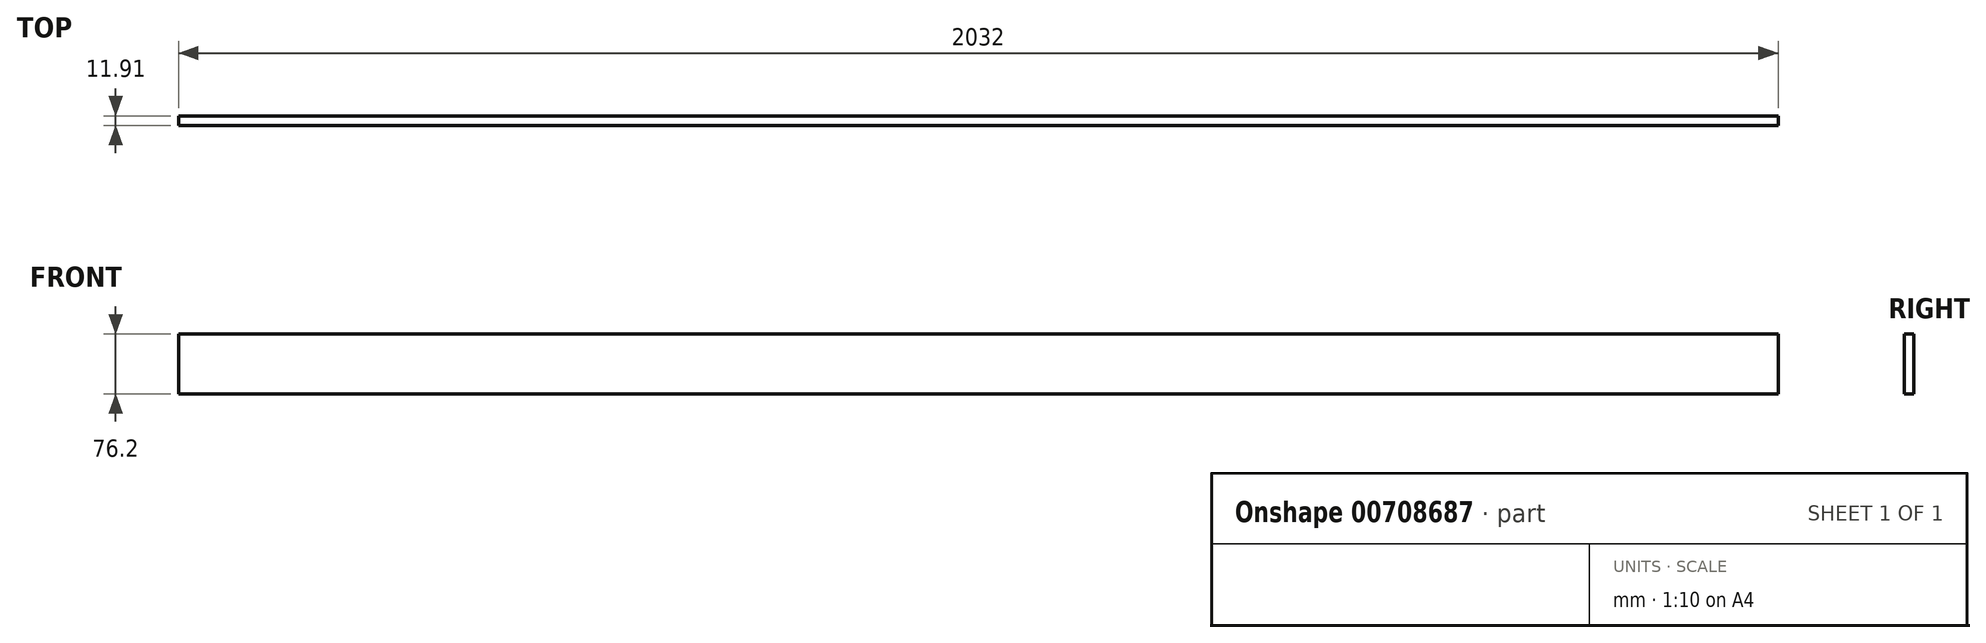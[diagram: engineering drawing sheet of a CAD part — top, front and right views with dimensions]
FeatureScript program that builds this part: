
annotation { "Feature Type Name" : "Feature", "Feature Type Description" : "" }
export const myFeature = defineFeature(function(context is Context, id is Id, definition is map)
    precondition{}
    {
        {
            var Q0;
            Q0=qCreatedBy(makeId("Front.planeOp"),FACE);
            var sketch = newSketch(context, id + "F0", { "sketchPlane" : qUnion([Q0])});
            skLineSegment(sketch, "E0.bottom", {"start": v(1016, -38.1) * mm, "end": v(-1016, -38.1) * mm});
            skLineSegment(sketch, "E0.top", {"start": v(1016, 38.1) * mm, "end": v(-1016, 38.1) * mm});
            skLineSegment(sketch, "E0.left", {"start": v(1016, -38.1) * mm, "end": v(1016, 38.1) * mm});
            skLineSegment(sketch, "E0.right", {"start": v(-1016, -38.1) * mm, "end": v(-1016, 38.1) * mm});
            skPoint(sketch, "E0.middle", {"position": v(0, 0) * mm});
            skSolve(sketch);
        }
        {
            var Q0;
            Q0=makeQuery(id+"F0.imprint","IMPRINT",FACE,{"disambiguationData":[TD([[makeQuery(id+"F0.imprint","IMPRINT",EDGE,{"derivedFrom":sQuery(id+"F0.wireOp",EDGE,"E0.bottom")}),-1.0]])]});
            extrude(context, id + "F1", {"entities" : qUnion([Q0]), "depth" : 11.9 * mm, "offsetDistance" : 25.4 * mm});
        }
    });
